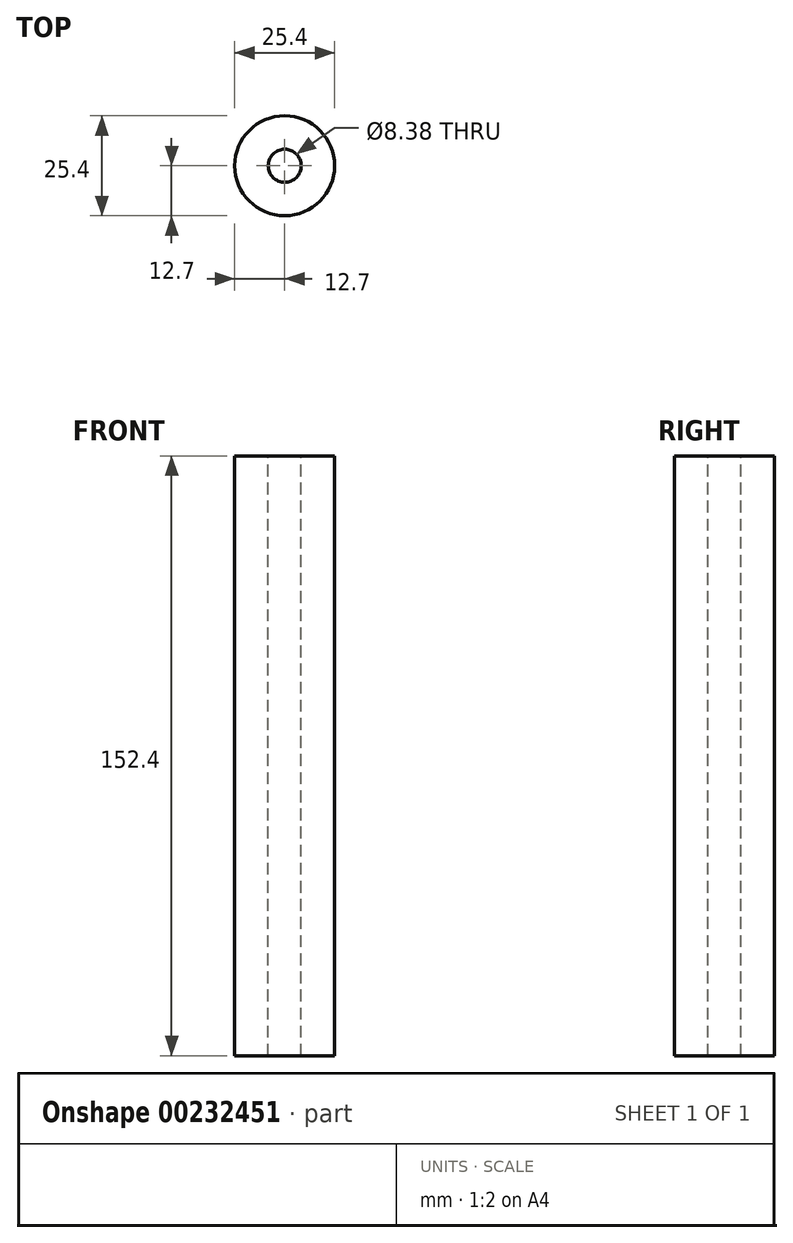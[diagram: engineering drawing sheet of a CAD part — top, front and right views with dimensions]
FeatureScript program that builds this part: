
annotation { "Feature Type Name" : "Feature", "Feature Type Description" : "" }
export const myFeature = defineFeature(function(context is Context, id is Id, definition is map)
    precondition{}
    {
        {
            var Q0;
            Q0=qCreatedBy(makeId("Top.planeOp"),FACE);
            var sketch = newSketch(context, id + "F0", { "sketchPlane" : qUnion([Q0])});
            skCircle(sketch, "E0", {"center": v(0, 0) * mm, "radius": 12.7 * mm});
            skSolve(sketch);
        }
        {
            var Q0;
            Q0 = qSketchRegion(id + "F0", true);
            extrude(context, id + "F1", {"entities" : qUnion([Q0]), "depth" : 152.4 * mm});
        }
        {
            var Q0;
            Q0=makeQuery(id+"F1.opExtrude","CAP_FACE",FACE,{"disambiguationData":[OSD([sQuery(id+"F0.wireOp",EDGE,"E0")])],"isStart":false});
            var sketch = newSketch(context, id + "F2", { "sketchPlane" : qUnion([Q0])});
            skSolve(sketch);
        }
        {
            var Q0;
            Q0=makeQuery(id+"F2.imprint","IMPRINT",FACE,{"disambiguationData":[TD([[makeQuery(id+"F2.imprint","IMPRINT",EDGE,{"derivedFrom":makeQuery(id+"F1.opExtrude","CAP_EDGE",EDGE,{"disambiguationData":[OSD([sQuery(id+"F0.wireOp",EDGE,"E0")])],"isStart":false})}),1.0]])]});
            var sketch = newSketch(context, id + "F3", { "sketchPlane" : qUnion([Q0])});
            skSolve(sketch);
        }
        {
            var Q0;
            Q0=makeQuery(id+"F3.imprint","IMPRINT",FACE,{"disambiguationData":[TD([[makeQuery(id+"F3.imprint","IMPRINT",EDGE,{"derivedFrom":makeQuery(id+"F2.imprint","IMPRINT",EDGE,{"derivedFrom":makeQuery(id+"F1.opExtrude","CAP_EDGE",EDGE,{"disambiguationData":[OSD([sQuery(id+"F0.wireOp",EDGE,"E0")])],"isStart":false})})}),1.0]])]});
            var sketch = newSketch(context, id + "F4", { "sketchPlane" : qUnion([Q0])});
            skCircle(sketch, "E1", {"center": v(0, 0) * mm, "radius": 4.2 * mm});
            skSolve(sketch);
        }
        {
            var Q0;
            Q0=makeQuery(id+"F4.imprint","IMPRINT",FACE,{"disambiguationData":[TD([[makeQuery(id+"F4.imprint","IMPRINT",EDGE,{"derivedFrom":sQuery(id+"F4.wireOp",EDGE,"E1")}),1.0]])]});
            var sketch = newSketch(context, id + "F5", { "sketchPlane" : qUnion([Q0])});
            skSolve(sketch);
        }
        {
            var Q0;
            Q0 = qSketchRegion(id + "F5", true);
            var Q1;
            Q1=makeQuery(id+"F5.imprint","IMPRINT",FACE,{"disambiguationData":[TD([[makeQuery(id+"F5.imprint","IMPRINT",EDGE,{"derivedFrom":makeQuery(id+"F4.imprint","IMPRINT",EDGE,{"derivedFrom":sQuery(id+"F4.wireOp",EDGE,"E1")})}),1.0]])]});
            extrude(context, id + "F6", {"entities" : qUnion([Q0, Q1]), "operationType" : NewBodyOperationType.REMOVE, "oppositeDirection" : true, "depth" : 254 * mm});
        }
    });
